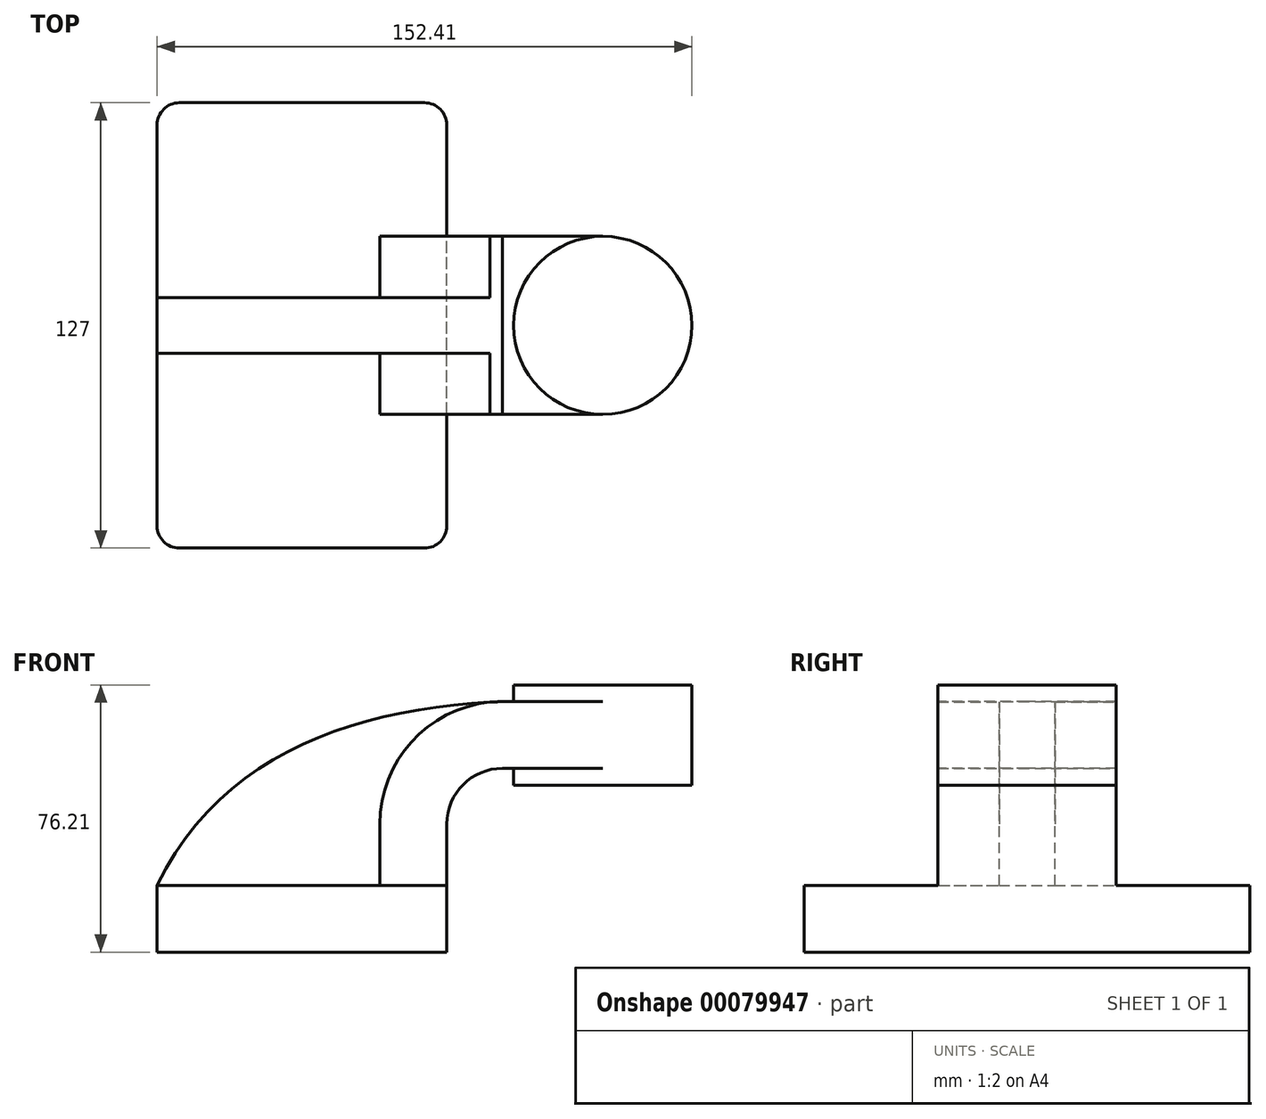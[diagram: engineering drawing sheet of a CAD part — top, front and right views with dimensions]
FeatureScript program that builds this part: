
annotation { "Feature Type Name" : "Feature", "Feature Type Description" : "" }
export const myFeature = defineFeature(function(context is Context, id is Id, definition is map)
    precondition{}
    {
        {
            var Q0;
            Q0=qCreatedBy(makeId("Front.planeOp"),FACE);
            var sketch = newSketch(context, id + "F0", { "sketchPlane" : qUnion([Q0])});
            skLineSegment(sketch, "E0.bottom", {"start": v(41.27, -9.52) * mm, "end": v(-41.27, -9.53) * mm});
            skLineSegment(sketch, "E0.top", {"start": v(41.27, 9.53) * mm, "end": v(-41.27, 9.52) * mm});
            skLineSegment(sketch, "E0.left", {"start": v(41.28, -9.52) * mm, "end": v(41.27, 9.53) * mm});
            skLineSegment(sketch, "E0.right", {"start": v(-41.27, -9.53) * mm, "end": v(-41.27, 9.52) * mm});
            skPoint(sketch, "E0.middle", {"position": v(0, 0) * mm});
            skLineSegment(sketch, "E1.bottom", {"start": v(111.12, 38.1) * mm, "end": v(60.32, 38.1) * mm});
            skLineSegment(sketch, "E1.top", {"start": v(111.12, 66.67) * mm, "end": v(60.32, 66.67) * mm});
            skLineSegment(sketch, "E1.left", {"start": v(111.12, 38.1) * mm, "end": v(111.12, 66.68) * mm});
            skLineSegment(sketch, "E1.right", {"start": v(60.32, 38.1) * mm, "end": v(60.32, 66.67) * mm});
            skPoint(sketch, "E1.middle", {"position": v(85.72, 52.39) * mm});
            skLineSegment(sketch, "E2", {"start": v(41.27, 9.53) * mm, "end": v(41.27, 27) * mm});
            skArc(sketch, "E3", {"start": v(41.27, 27) * mm, "mid": v(45.92, 38.23) * mm, "end": v(57.15, 42.88) * mm});
            skLineSegment(sketch, "E4", {"start": v(57.15, 42.88) * mm, "end": v(85.72, 42.88) * mm});
            skLineSegment(sketch, "E5.0", {"start": v(57.15, 61.93) * mm, "end": v(85.72, 61.93) * mm});
            skArc(sketch, "E5.1", {"start": v(22.22, 27) * mm, "mid": v(32.45, 51.7) * mm, "end": v(57.15, 61.93) * mm});
            skLineSegment(sketch, "E5.2", {"start": v(22.22, 9.53) * mm, "end": v(22.22, 27) * mm});
            skLineSegment(sketch, "E6", {"start": v(85.72, 38.1) * mm, "end": v(85.72, 66.67) * mm});
            skFitSpline(sketch, "E7", {"points": [v(-41.27, 9.52) * mm, v(57.15, 61.93) * mm], "startDerivative": vector(55.78, 114.99) * mm, "endDerivative": vector(122.99, 5.38) * mm});
            skSolve(sketch);
        }
        {
            var Q0;
            Q0=makeQuery(id+"F0.imprint","IMPRINT",FACE,{"disambiguationData":[TD([[makeQuery(id+"F0.imprint","IMPRINT",EDGE,{"derivedFrom":sQuery(id+"F0.wireOp",EDGE,"E0.bottom")}),-1.0]])]});
            extrude(context, id + "F1", {"entities" : qUnion([Q0]), "endBound" : BoundingType.SYMMETRIC, "depth" : (5 * 25.4) * mm});
        }
        {
            var Q0;
            {var subQ1=sQuery(id+"F0.wireOp",EDGE,"E2");Q0=makeQuery(id+"F0.imprint","IMPRINT",FACE,{"disambiguationData":[TD([[makeQuery(id+"F0.imprint","IMPRINT",EDGE,{"derivedFrom":subQ1}),1.0]])]});}
            var Q1;
            {var subQ0=sQuery(id+"F0.wireOp",EDGE,"E4");var subQ1=sQuery(id+"F0.wireOp",EDGE,"E1.right");var subQ2=makeQuery(id+"F0.imprint","INTERSECT",VERTEX,{"derivedFrom":[subQ1,subQ0]});Q1=makeQuery(id+"F0.imprint","IMPRINT",FACE,{"disambiguationData":[TD([[makeQuery(id+"F0.imprint","IMPRINT",EDGE,{"disambiguationData":[TD([[subQ2,-1.0]])],"derivedFrom":subQ1}),-1.0]])]});}
            extrude(context, id + "F2", {"entities" : qUnion([Q0, Q1]), "operationType" : NewBodyOperationType.ADD, "endBound" : BoundingType.SYMMETRIC, "depth" : 50.8 * mm});
        }
        {
            var Q0;
            {var subQ3=sQuery(id+"F0.wireOp",EDGE,"E5.2");Q0=makeQuery(id+"F0.imprint","IMPRINT",FACE,{"disambiguationData":[TD([[makeQuery(id+"F0.imprint","IMPRINT",EDGE,{"derivedFrom":subQ3}),1.0]])]});}
            extrude(context, id + "F3", {"entities" : qUnion([Q0]), "operationType" : NewBodyOperationType.ADD, "endBound" : BoundingType.SYMMETRIC, "depth" : (.625 * 25.4) * mm});
        }
        {
            var Q0;
            {var subQ0=sQuery(id+"F0.wireOp",EDGE,"E1.left");Q0=makeQuery(id+"F0.imprint","IMPRINT",FACE,{"disambiguationData":[TD([[makeQuery(id+"F0.imprint","IMPRINT",EDGE,{"derivedFrom":subQ0}),1.0]])]});}
            var Q1;
            Q1=sQuery(id+"F0.wireOp",EDGE,"E6");
            revolve(context, id + "F4", {"operationType" : NewBodyOperationType.ADD, "entities" : qUnion([Q0]), "axis" : qUnion([Q1]), "revolveType" : RevolveType.FULL});
        }
        {
            var Q0;
            Q0=makeQuery(id+"F1.opExtrude","CAP_EDGE",EDGE,{"disambiguationData":[OSD([sQuery(id+"F0.wireOp",EDGE,"E0.left")])],"isStart":false});
            var Q1;
            Q1=makeQuery(id+"F1.opExtrude","CAP_EDGE",EDGE,{"disambiguationData":[OSD([sQuery(id+"F0.wireOp",EDGE,"E0.right")])],"isStart":false});
            var Q2;
            Q2=makeQuery(id+"F1.opExtrude","CAP_EDGE",EDGE,{"disambiguationData":[OSD([sQuery(id+"F0.wireOp",EDGE,"E0.left")])],"isStart":true});
            var Q3;
            Q3=makeQuery(id+"F1.opExtrude","CAP_EDGE",EDGE,{"disambiguationData":[OSD([sQuery(id+"F0.wireOp",EDGE,"E0.right")])],"isStart":true});
            fillet(context, id + "F5", {"entities" : qUnion([Q0, Q1, Q2, Q3]), "radius" : (.25 * 25.4) * mm, "tangentPropagation" : true, "allowEdgeOverflow" : false});
        }
    });
